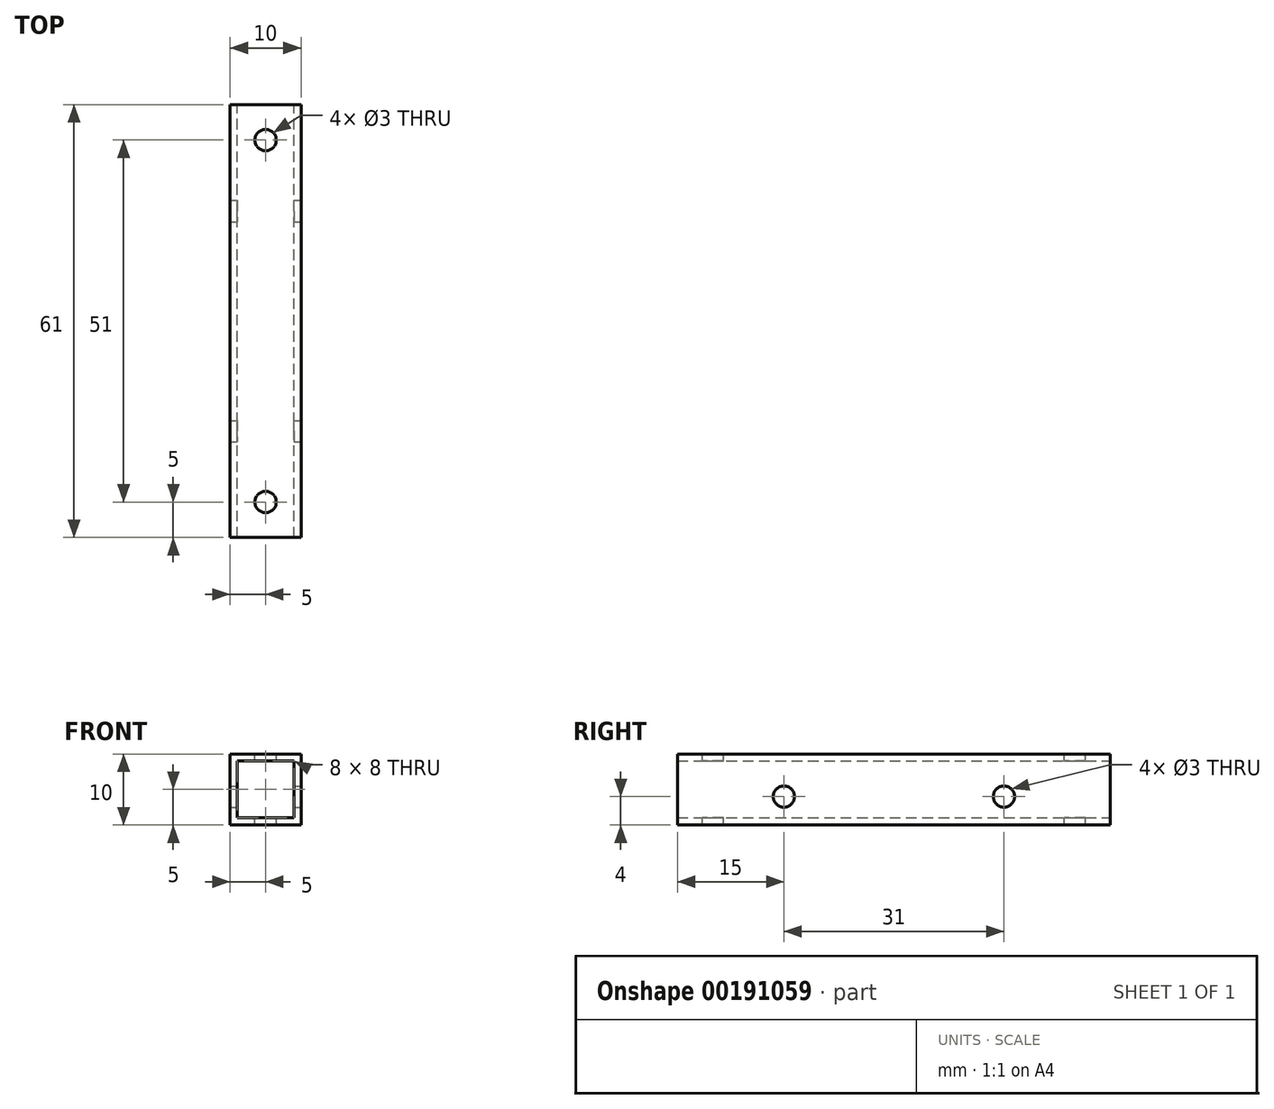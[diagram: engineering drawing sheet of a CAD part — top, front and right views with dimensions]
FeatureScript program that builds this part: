
annotation { "Feature Type Name" : "Feature", "Feature Type Description" : "" }
export const myFeature = defineFeature(function(context is Context, id is Id, definition is map)
    precondition{}
    {
        {
            var Q0;
            Q0=qCreatedBy(makeId("Front.planeOp"),FACE);
            var sketch = newSketch(context, id + "F0", { "sketchPlane" : qUnion([Q0])});
            skLineSegment(sketch, "E0.bottom", {"start": v(-5, -5) * mm, "end": v(5, -5) * mm});
            skLineSegment(sketch, "E0.top", {"start": v(-5, 5) * mm, "end": v(5, 5) * mm});
            skLineSegment(sketch, "E0.left", {"start": v(-5, -5) * mm, "end": v(-5, 5) * mm});
            skLineSegment(sketch, "E0.right", {"start": v(5, -5) * mm, "end": v(5, 5) * mm});
            skPoint(sketch, "E0.middle", {"position": v(0, 0) * mm});
            skLineSegment(sketch, "E1.bottom", {"start": v(-4, -4) * mm, "end": v(4, -4) * mm});
            skLineSegment(sketch, "E1.top", {"start": v(-4, 4) * mm, "end": v(4, 4) * mm});
            skLineSegment(sketch, "E1.left", {"start": v(-4, -4) * mm, "end": v(-4, 4) * mm});
            skLineSegment(sketch, "E1.right", {"start": v(4, -4) * mm, "end": v(4, 4) * mm});
            skSolve(sketch);
        }
        {
            var Q0;
            Q0 = qSketchRegion(id + "F0", true);
            extrude(context, id + "F1", {"entities" : qUnion([Q0]), "depth" : 61 * mm});
        }
        {
            var Q0;
            Q0=makeQuery(id+"F1.opExtrude","SWEPT_FACE",FACE,{"disambiguationData":[OSD([sQuery(id+"F0.wireOp",EDGE,"E0.top")])]});
            var sketch = newSketch(context, id + "F2", { "sketchPlane" : qUnion([Q0])});
            skLineSegment(sketch, "E2", {"start": v(0, 0) * mm, "end": v(0, -61) * mm, "construction": true});
            skLineSegment(sketch, "E3", {"start": v(-5, -30.5) * mm, "end": v(5, -30.5) * mm, "construction": true});
            skCircle(sketch, "E4", {"center": v(0, -5) * mm, "radius": 1.5 * mm});
            skCircle(sketch, "E5.MirrorC", {"center": v(0, -56) * mm, "radius": 1.5 * mm});
            skSolve(sketch);
        }
        {
            var Q0;
            Q0 = qSketchRegion(id + "F2", true);
            extrude(context, id + "F3", {"entities" : qUnion([Q0]), "operationType" : NewBodyOperationType.REMOVE, "oppositeDirection" : true, "depth" : 25 * mm});
        }
        {
            var Q0;
            Q0=makeQuery(id+"F1.opExtrude","SWEPT_FACE",FACE,{"disambiguationData":[OSD([sQuery(id+"F0.wireOp",EDGE,"E0.right")])]});
            var sketch = newSketch(context, id + "F4", { "sketchPlane" : qUnion([Q0])});
            skLineSegment(sketch, "E6", {"start": v(-30.5, 5) * mm, "end": v(-30.5, -5) * mm, "construction": true});
            skCircle(sketch, "E7", {"center": v(-15, -1) * mm, "radius": 1.5 * mm});
            skCircle(sketch, "E8.MirrorC", {"center": v(-46, -1) * mm, "radius": 1.5 * mm});
            skSolve(sketch);
        }
        {
            var Q0;
            Q0 = qSketchRegion(id + "F4", true);
            extrude(context, id + "F5", {"entities" : qUnion([Q0]), "operationType" : NewBodyOperationType.REMOVE, "oppositeDirection" : true, "depth" : 25 * mm});
        }
    });
